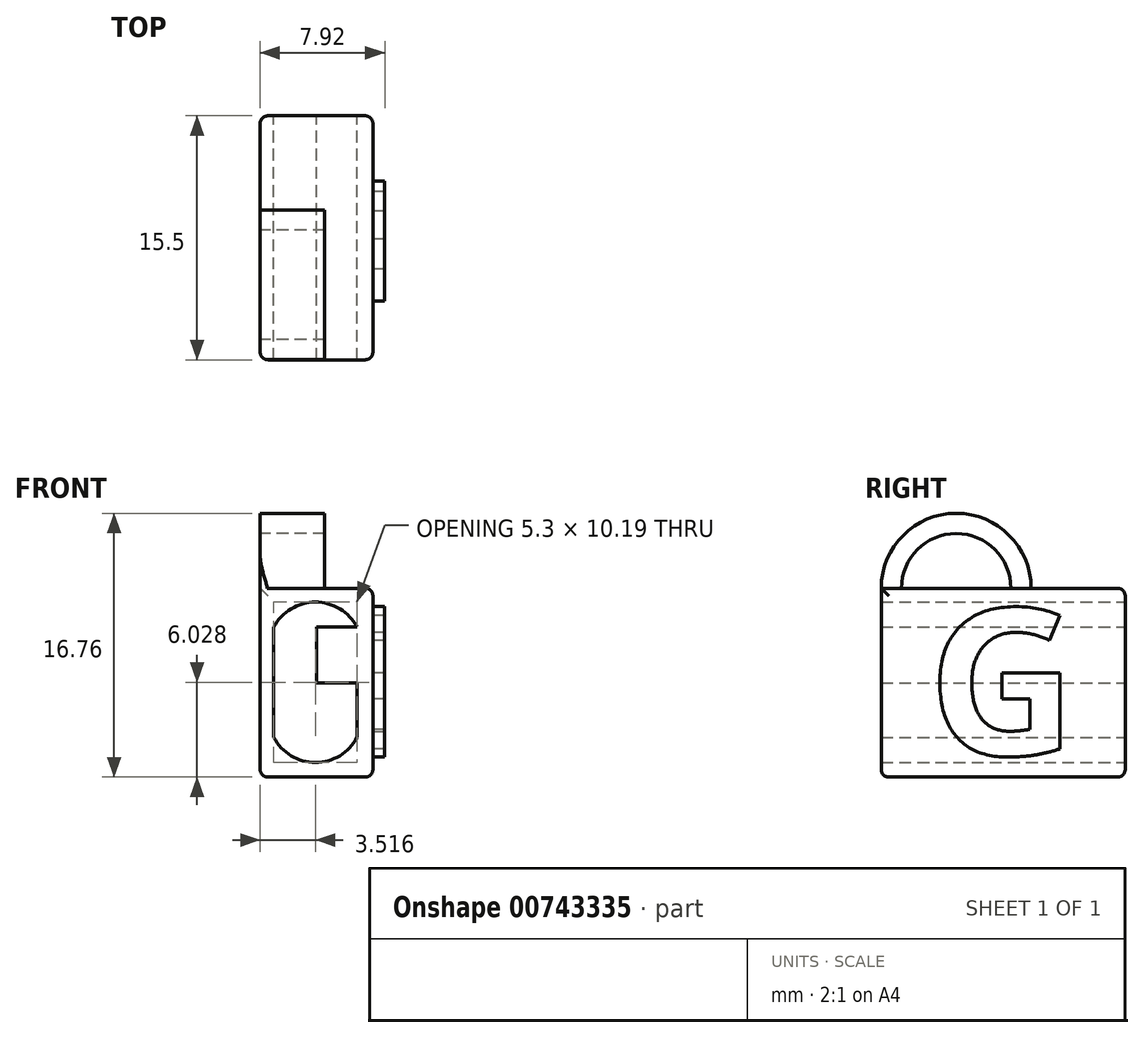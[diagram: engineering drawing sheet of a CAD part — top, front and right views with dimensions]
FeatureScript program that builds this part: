
annotation { "Feature Type Name" : "Feature", "Feature Type Description" : "" }
export const myFeature = defineFeature(function(context is Context, id is Id, definition is map)
    precondition{}
    {
        {
            var Q0;
            Q0=qCreatedBy(makeId("Right.planeOp"),FACE);
            var sketch = newSketch(context, id + "F0", { "sketchPlane" : qUnion([Q0])});
            skLineSegment(sketch, "E0.bottom", {"start": v(-7.75, 6) * mm, "end": v(7.75, 6) * mm});
            skLineSegment(sketch, "E0.top", {"start": v(-7.75, -6) * mm, "end": v(7.75, -6) * mm});
            skLineSegment(sketch, "E0.left", {"start": v(-7.75, 6) * mm, "end": v(-7.75, -6) * mm});
            skLineSegment(sketch, "E0.right", {"start": v(7.75, 6) * mm, "end": v(7.75, -6) * mm});
            skPoint(sketch, "E0.middle", {"position": v(0, 0) * mm});
            skCircle(sketch, "E1", {"center": v(-2.99, 6) * mm, "radius": 4.76 * mm});
            skCircle(sketch, "E2", {"center": v(-2.99, 6) * mm, "radius": 3.48 * mm});
            skLineSegment(sketch, "E3", {"start": v(-7.75, 6) * mm, "end": v(1.77, 6) * mm});
            skSolve(sketch);
        }
        {
            var Q0;
            Q0=makeQuery(id+"F0.imprint","IMPRINT",FACE,{"disambiguationData":[TD([[makeQuery(id+"F0.imprint","IMPRINT",EDGE,{"derivedFrom":sQuery(id+"F0.wireOp",EDGE,"E0.top")}),1.0]])]});
            var Q1;
            {var subQ0=sQuery(id+"F0.wireOp",EDGE,"E1");var subQ1=sQuery(id+"F0.wireOp",EDGE,"E0.bottom");var subQ2=makeQuery(id+"F0.imprint","INTERSECT",VERTEX,{"disambiguationData":[OD(1.0)],"derivedFrom":[subQ1,subQ0]});Q1=makeQuery(id+"F0.imprint","IMPRINT",FACE,{"disambiguationData":[TD([[makeQuery(id+"F0.imprint","IMPRINT",EDGE,{"disambiguationData":[TD([[subQ2,1.0]])],"derivedFrom":subQ1}),-1.0]])]});}
            var Q2;
            {var subQ0=sQuery(id+"F0.wireOp",EDGE,"E2");var subQ1=sQuery(id+"F0.wireOp",EDGE,"E0.bottom");var subQ2=makeQuery(id+"F0.imprint","INTERSECT",VERTEX,{"disambiguationData":[OD(0.0)],"derivedFrom":[subQ1,subQ0]});Q2=makeQuery(id+"F0.imprint","IMPRINT",FACE,{"disambiguationData":[TD([[makeQuery(id+"F0.imprint","IMPRINT",EDGE,{"disambiguationData":[TD([[subQ2,-1.0]])],"derivedFrom":subQ1}),-1.0]])]});}
            var Q3;
            Q3 = qSketchRegion(id + "F2", true);
            extrude(context, id + "F1", {"entities" : qUnion([Q0, Q1, Q2, Q3]), "depth" : 7.17 * mm, "offsetDistance" : 25 * mm});
        }
        {
            var Q0;
            Q0=makeQuery(id+"F1.opExtrude","SWEPT_FACE",FACE,{"disambiguationData":[OSD([sQuery(id+"F0.wireOp",EDGE,"E0.right")])]});
            var sketch = newSketch(context, id + "F2", { "sketchPlane" : qUnion([Q0])});
            skLineSegment(sketch, "E4", {"start": v(-3.58, 6) * mm, "end": v(-3.58, -6) * mm});
            skLineSegment(sketch, "E5", {"start": v(-7.17, 0) * mm, "end": v(0, 0) * mm});
            skPoint(sketch, "E6.middle", {"position": v(-1.35, 0.03) * mm});
            skPoint(sketch, "E6.middle.positionSnap0", {"position": v(-6.17, 0.03) * mm});
            skPoint(sketch, "E6.centerSnap0", {"position": v(-6.17, 0.03) * mm});
            skLineSegment(sketch, "E7", {"start": v(-6.17, 3.53) * mm, "end": v(-0.87, 3.53) * mm});
            skLineSegment(sketch, "E8", {"start": v(-6.17, -3.47) * mm, "end": v(-0.87, -3.47) * mm});
            skLineSegment(sketch, "E9", {"start": v(-6.17, 3.53) * mm, "end": v(-3.52, 3.53) * mm});
            skArc(sketch, "E10", {"start": v(-0.87, 3.53) * mm, "mid": v(-3.52, 5.12) * mm, "end": v(-6.17, 3.53) * mm});
            skArc(sketch, "E11", {"start": v(-6.17, -3.47) * mm, "mid": v(-3.52, -5.07) * mm, "end": v(-0.87, -3.47) * mm});
            skLineSegment(sketch, "E12", {"start": v(-6.17, 3.53) * mm, "end": v(-6.17, -3.47) * mm});
            skLineSegment(sketch, "E13", {"start": v(-0.87, 3.53) * mm, "end": v(-0.87, -3.47) * mm});
            skSolve(sketch);
        }
        {
            var Q0;
            {var subQ0=sQuery(id+"F2.wireOp",EDGE,"E10");var subQ1=sQuery(id+"F2.wireOp",EDGE,"E4");var subQ2=makeQuery(id+"F2.imprint","INTERSECT",VERTEX,{"derivedFrom":[subQ1,subQ0]});Q0=makeQuery(id+"F2.imprint","IMPRINT",FACE,{"disambiguationData":[TD([[makeQuery(id+"F2.imprint","IMPRINT",EDGE,{"disambiguationData":[TD([[subQ2,-1.0]])],"derivedFrom":subQ1}),-1.0]])]});}
            var Q1;
            {var subQ5=sQuery(id+"F2.wireOp",EDGE,"E7");Q1=makeQuery(id+"F2.imprint","IMPRINT",FACE,{"disambiguationData":[TD([[makeQuery(id+"F2.imprint","IMPRINT",EDGE,{"derivedFrom":subQ5}),1.0]])]});}
            var Q2;
            {var subQ1=sQuery(id+"F2.wireOp",EDGE,"E7");Q2=makeQuery(id+"F2.imprint","IMPRINT",FACE,{"disambiguationData":[TD([[makeQuery(id+"F2.imprint","IMPRINT",EDGE,{"derivedFrom":subQ1}),-1.0]])]});}
            var Q3;
            {var subQ0=sQuery(id+"F2.wireOp",EDGE,"E9");var subQ1=sQuery(id+"F2.wireOp",EDGE,"E4");var subQ2=makeQuery(id+"F2.imprint","INTERSECT",VERTEX,{"derivedFrom":[subQ1,subQ0]});Q3=makeQuery(id+"F2.imprint","IMPRINT",FACE,{"disambiguationData":[TD([[makeQuery(id+"F2.imprint","IMPRINT",EDGE,{"disambiguationData":[TD([[subQ2,-1.0]])],"derivedFrom":subQ1}),-1.0]])]});}
            var Q4;
            {var subQ0=sQuery(id+"F2.wireOp",EDGE,"E5");var subQ1=sQuery(id+"F2.wireOp",EDGE,"E4");var subQ2=makeQuery(id+"F2.imprint","INTERSECT",VERTEX,{"derivedFrom":[subQ1,subQ0]});Q4=makeQuery(id+"F2.imprint","IMPRINT",FACE,{"disambiguationData":[TD([[makeQuery(id+"F2.imprint","IMPRINT",EDGE,{"disambiguationData":[TD([[subQ2,-1.0]])],"derivedFrom":subQ1}),-1.0]])]});}
            var Q5;
            {var subQ0=sQuery(id+"F2.wireOp",EDGE,"E5");var subQ1=sQuery(id+"F2.wireOp",EDGE,"E4");var subQ2=makeQuery(id+"F2.imprint","INTERSECT",VERTEX,{"derivedFrom":[subQ1,subQ0]});Q5=makeQuery(id+"F2.imprint","IMPRINT",FACE,{"disambiguationData":[TD([[makeQuery(id+"F2.imprint","IMPRINT",EDGE,{"disambiguationData":[TD([[subQ2,-1.0]])],"derivedFrom":subQ1}),1.0]])]});}
            var Q6;
            {var subQ0=sQuery(id+"F2.wireOp",EDGE,"E8");var subQ1=sQuery(id+"F2.wireOp",EDGE,"E4");var subQ2=makeQuery(id+"F2.imprint","INTERSECT",VERTEX,{"derivedFrom":[subQ1,subQ0]});Q6=makeQuery(id+"F2.imprint","IMPRINT",FACE,{"disambiguationData":[TD([[makeQuery(id+"F2.imprint","IMPRINT",EDGE,{"disambiguationData":[TD([[subQ2,-1.0]])],"derivedFrom":subQ1}),1.0]])]});}
            var Q7;
            {var subQ0=sQuery(id+"F2.wireOp",EDGE,"E8");var subQ1=sQuery(id+"F2.wireOp",EDGE,"E4");var subQ2=makeQuery(id+"F2.imprint","INTERSECT",VERTEX,{"derivedFrom":[subQ1,subQ0]});Q7=makeQuery(id+"F2.imprint","IMPRINT",FACE,{"disambiguationData":[TD([[makeQuery(id+"F2.imprint","IMPRINT",EDGE,{"disambiguationData":[TD([[subQ2,-1.0]])],"derivedFrom":subQ1}),-1.0]])]});}
            extrude(context, id + "F3", {"entities" : qUnion([Q0, Q1, Q2, Q3, Q4, Q5, Q6, Q7]), "operationType" : NewBodyOperationType.REMOVE, "oppositeDirection" : true, "depth" : 25 * mm, "offsetDistance" : 25 * mm});
        }
        {
            var Q0;
            {var subQ0=sQuery(id+"F0.wireOp",EDGE,"E1");var subQ1=sQuery(id+"F0.wireOp",EDGE,"E0.bottom");var subQ2=makeQuery(id+"F0.imprint","INTERSECT",VERTEX,{"disambiguationData":[OD(1.0)],"derivedFrom":[subQ1,subQ0]});Q0=makeQuery(id+"F0.imprint","IMPRINT",FACE,{"disambiguationData":[TD([[makeQuery(id+"F0.imprint","IMPRINT",EDGE,{"disambiguationData":[TD([[subQ2,1.0]])],"derivedFrom":subQ1}),1.0]])]});}
            extrude(context, id + "F4", {"entities" : qUnion([Q0]), "operationType" : NewBodyOperationType.ADD, "depth" : 4.1 * mm, "offsetDistance" : 25 * mm});
        }
        {
            var Q0;
            Q0=makeQuery(id+"F1.opExtrude","CAP_EDGE",EDGE,{"disambiguationData":[OSD([sQuery(id+"F0.wireOp",EDGE,"E0.left")])],"isStart":false});
            var Q1;
            Q1=makeQuery(id+"F1.opExtrude","CAP_EDGE",EDGE,{"disambiguationData":[OSD([sQuery(id+"F0.wireOp",EDGE,"E0.left")])],"isStart":true});
            var Q2;
            Q2=makeQuery(id+"F1.opExtrude","SWEPT_EDGE",EDGE,{"disambiguationData":[OSD([sQuery(id+"F0.wireOp",EDGE,"E0.top"),sQuery(id+"F0.wireOp",EDGE,"E0.left")])]});
            var Q3;
            Q3=makeQuery(id+"F1.opExtrude","CAP_EDGE",EDGE,{"disambiguationData":[OSD([sQuery(id+"F0.wireOp",EDGE,"E0.bottom")])],"isStart":false});
            var Q4;
            Q4=makeQuery(id+"F1.opExtrude","CAP_EDGE",EDGE,{"disambiguationData":[OSD([sQuery(id+"F0.wireOp",EDGE,"E0.top")])],"isStart":false});
            var Q5;
            Q5=makeQuery(id+"F1.opExtrude","CAP_EDGE",EDGE,{"disambiguationData":[OSD([sQuery(id+"F0.wireOp",EDGE,"E0.right")])],"isStart":false});
            var Q6;
            Q6=makeQuery(id+"F1.opExtrude","CAP_EDGE",EDGE,{"disambiguationData":[OSD([sQuery(id+"F0.wireOp",EDGE,"E0.right")])],"isStart":true});
            var Q7;
            Q7=makeQuery(id+"F1.opExtrude","CAP_EDGE",EDGE,{"disambiguationData":[OSD([sQuery(id+"F0.wireOp",EDGE,"E0.top")])],"isStart":true});
            var Q8;
            Q8=makeQuery(id+"F1.opExtrude","SWEPT_EDGE",EDGE,{"disambiguationData":[OSD([sQuery(id+"F0.wireOp",EDGE,"E0.top"),sQuery(id+"F0.wireOp",EDGE,"E0.right")])]});
            var Q9;
            Q9=makeQuery(id+"F1.opExtrude","SWEPT_EDGE",EDGE,{"disambiguationData":[OSD([sQuery(id+"F0.wireOp",EDGE,"E0.bottom"),sQuery(id+"F0.wireOp",EDGE,"E0.right")])]});
            fillet(context, id + "F5", {"entities" : qUnion([Q0, Q1, Q2, Q3, Q4, Q5, Q6, Q7, Q8, Q9]), "radius" : 0.5 * mm, "tangentPropagation" : true, "allowEdgeOverflow" : false});
        }
        {
            var Q0;
            Q0=makeQuery(id+"F1.opExtrude","CAP_FACE",FACE,{"disambiguationData":[OSD([sQuery(id+"F0.wireOp",EDGE,"E0.bottom"),sQuery(id+"F0.wireOp",EDGE,"E0.top"),sQuery(id+"F0.wireOp",EDGE,"E0.left"),sQuery(id+"F0.wireOp",EDGE,"E0.right")])],"isStart":false});
            var sketch = newSketch(context, id + "F6", { "sketchPlane" : qUnion([Q0])});
            skText(sketch, "E14", { "text": "G", "fontName": "OpenSans-Bold.ttf"});
            const initialGuessF6  = {"E14": [-0.00478, -0.0046, 1, 0, 0.00938]};
            skSetInitialGuess(sketch, initialGuessF6);
            skSolve(sketch);
        }
        {
            var Q0;
            Q0=makeQuery(id+"F6.imprint","IMPRINT",FACE,{"disambiguationData":[TD([[makeQuery(id+"F6.imprint","IMPRINT",EDGE,{"derivedFrom":sQuery(id+"F6.wireOp",EDGE,"E14.sketch_text.stroke-0")}),-1.0]])]});
            extrude(context, id + "F7", {"entities" : qUnion([Q0]), "operationType" : NewBodyOperationType.ADD, "depth" : 0.75 * mm, "offsetDistance" : 25 * mm});
        }
    });
